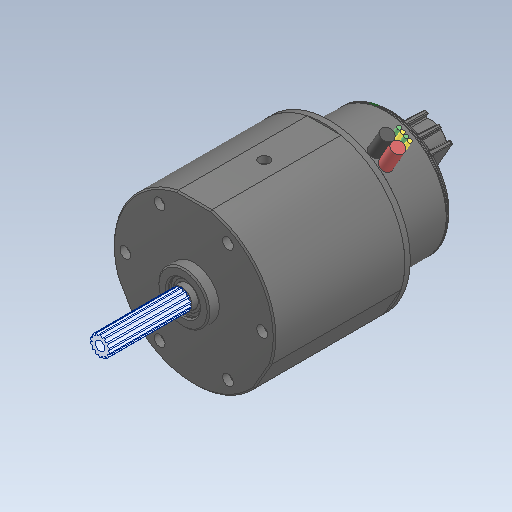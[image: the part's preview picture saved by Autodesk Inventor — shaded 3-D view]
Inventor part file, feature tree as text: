
AUTODESK INVENTOR PART (.ipt)
format: ipt  version: 2020 (Build 240168000, 168)  size: 1,374,720 bytes
history: native  units: in
note: dims shown in document units (in); Inventor stores cm internally (conversion verified against a paired STEP export)
features: fillet x4, other x2, chamfer x1
ambient origin geometry x8: Origin, YZ Plane, XZ Plane, XY Plane, X Axis, Y Axis, Z Axis, Center Point
bodies: Solid1 (feature_tree), Solid2 (feature_tree), Solid3 (feature_tree), Solid4 (feature_tree), Solid5 (feature_tree), Solid6 (feature_tree), Solid7 (feature_tree)
feature tree (7):
  chamfer  "Chamfer3"  [1 undecoded]
  other  "Boss-Extrude10"
  fillet  "Fillet4"  [1 undecoded]
  fillet  "Fillet3"  [1 undecoded]
  fillet  "Fillet5"  [1 undecoded]
  fillet  "Fillet6"  [1 undecoded]
  other  "#8-32 Tapped Hole1"
note: 5 required parameter values undecoded (feature->parameter linkage not recoverable at this tier; creation-order binding heuristic only, values carry confidence <= 0.55)
